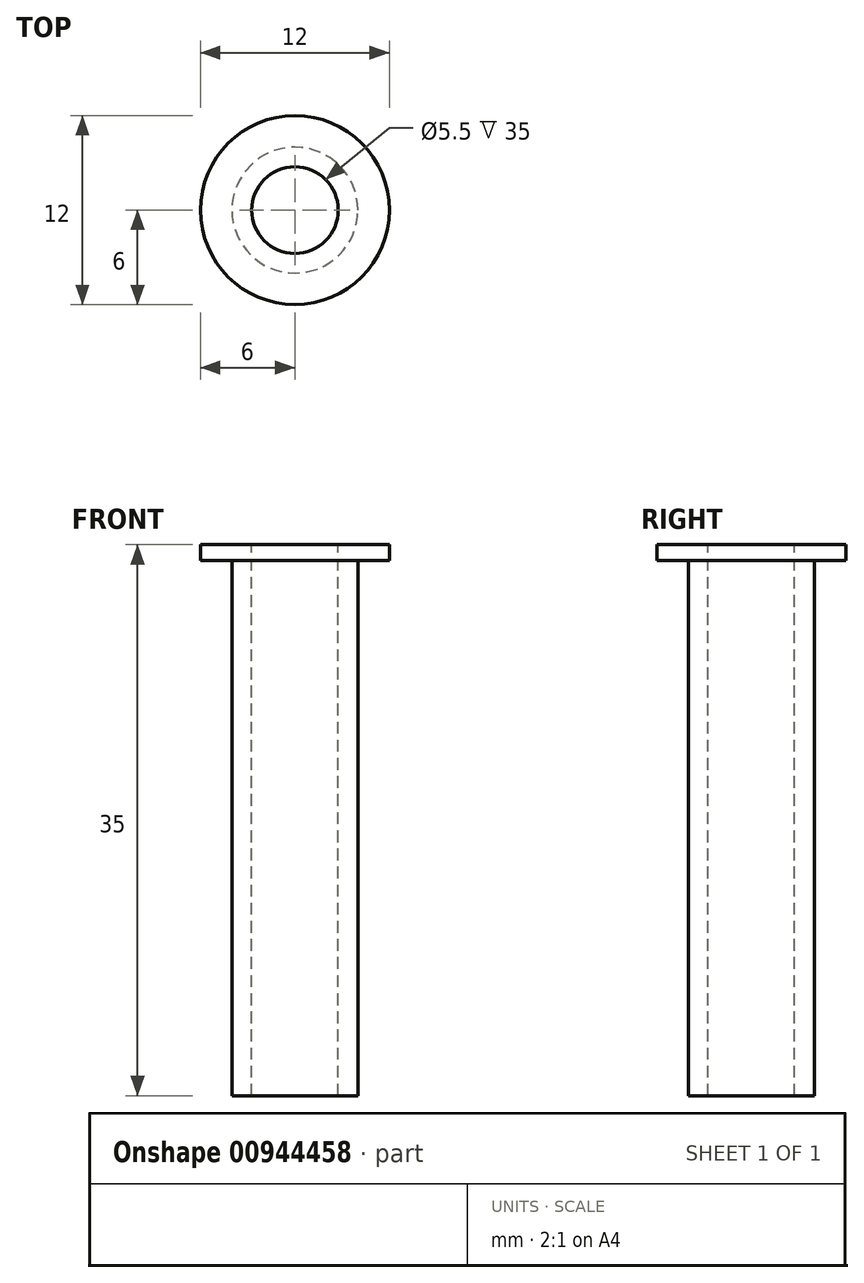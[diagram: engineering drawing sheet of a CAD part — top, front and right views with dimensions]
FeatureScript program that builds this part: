
annotation { "Feature Type Name" : "Feature", "Feature Type Description" : "" }
export const myFeature = defineFeature(function(context is Context, id is Id, definition is map)
    precondition{}
    {
        {
            var Q0;
            Q0=qCreatedBy(makeId("Top.planeOp"),FACE);
            var sketch = newSketch(context, id + "F0", { "sketchPlane" : qUnion([Q0])});
            skCircle(sketch, "E0", {"center": v(0, 0) * mm, "radius": 6 * mm});
            skSolve(sketch);
        }
        {
            var Q0;
            Q0 = qSketchRegion(id + "F0", true);
            extrude(context, id + "F1", {"entities" : qUnion([Q0]), "oppositeDirection" : true, "depth" : 1 * mm, "offsetDistance" : 25 * mm});
        }
        {
            var Q0;
            Q0=makeQuery(id+"F1.opExtrude","CAP_FACE",FACE,{"disambiguationData":[OSD([sQuery(id+"F0.wireOp",EDGE,"E0")])],"isStart":false});
            var sketch = newSketch(context, id + "F2", { "sketchPlane" : qUnion([Q0])});
            skCircle(sketch, "E1", {"center": v(0, 0) * mm, "radius": 4 * mm});
            skSolve(sketch);
        }
        {
            var Q0;
            Q0 = qSketchRegion(id + "F2", true);
            extrude(context, id + "F3", {"entities" : qUnion([Q0]), "operationType" : NewBodyOperationType.ADD, "depth" : 34 * mm, "offsetDistance" : 25 * mm});
        }
        {
            var Q0;
            Q0=makeQuery(id+"F1.opExtrude","CAP_FACE",FACE,{"disambiguationData":[OSD([sQuery(id+"F0.wireOp",EDGE,"E0")])],"isStart":true});
            var sketch = newSketch(context, id + "F4", { "sketchPlane" : qUnion([Q0])});
            skCircle(sketch, "E2", {"center": v(0, 0) * mm, "radius": 2.75 * mm});
            skSolve(sketch);
        }
        {
            var Q0;
            Q0 = qSketchRegion(id + "F4", true);
            extrude(context, id + "F5", {"entities" : qUnion([Q0]), "operationType" : NewBodyOperationType.REMOVE, "oppositeDirection" : true, "depth" : 35 * mm, "offsetDistance" : 25 * mm});
        }
    });
